# Revit family: 0048949
name_source: partatom
category: Lighting Fixtures
revit_build: Autodesk Revit 2017 (Build: 20190507_1515(x64)
units: mm (PartAtom-declared; Revit-internal decimal feet)

## family parameters
Cut with Voids When Loaded = No
Host = Face
Light Source = Yes
OmniClass Number = 23.80.70.00
OmniClass Title = Lighting
Part Type = Normal
Room Calculation Point = No
Round Connector Dimension = Use Diameter
Shared = No

## types (6) — shared parameters
Assembly Code = D5020200
AssetType = Fixed
ClassificationName = Uniclass2015
ClassificationValue = EF_70_80
Color Filter = 16777215
Default Elevation = 1219 mm
Dimming Lamp Color Temperature Shift = <None>
DocumentationLiterature = http://www.sylvania-lighting.com
ElectricShockClassification = Class I
Emit Shape Visible in Rendering = No
Emit from Circle Diameter = 610 mm
GAP_SYL = 3 mm  [stored 0.00984252 ft]
HEIGHT_SYL = 77 mm
HOLE_HEIGHT_SYL = 24 mm
IfcExportAs = IfcLightFixtureType
IfcExportType = IfcLightFixtureType
ImpactProtectionIndex = IK08
IngressProtection = IP20
Keynote = 16500
LUM_R_SYL = 30 mm  [stored 0.0984252 ft]
Lamp = LED
LampColourRenderingIndex = 80
LampColourTemperature = 4000 K
LampMacAdamStep = 5
LampsType = LED
Manufacturer = Feilo Sylvania
ManufacturerName = Feilo Sylvania
Material = steel housing, pc polycarbonate diffuser
Material_1_SYL = Dynamo
Material_2_SYL = <By Category>
Material_3_SYL = <By Category>
Material_4_SYL = <By Category>
NominalDepth = 70 mm
NominalHeight = 77 mm
NominalLength = 672 mm
PowerFactor = 0.9
R_HEIGHT_SYL = 44 mm
Tilt Angle = -90.00°
Type Image = <None>
URL = http://www.sylvania-lighting.com
Voltage = 0 V
WIDTH/2_SYL = 35 mm  [stored 0.114829 ft]
zero-valued in all types: Cost

## per-type parameters (varying)
| type | Apparent Load | Description | LampNominalLuminous | LuminousEfficacy | Model | ModelNumber | ModelReference | Name | Photometric Web File | PowerConsumption | TypeName | Weight |
| 0048951 WAYLINE 600 MWCOR 1200LM 840 | 10 VA | LED batten, T8 replacement, ease of installation through 2 part push-in design of the housing (safety cable included), through wiring capability, steel housing, 1200lm, 10W, 120lm/W, 4000K, CRI80, 3 step MacAdam ellipse, symmetric wide beam angle, Class I, 90000 hrs L80B20 lifespan, non-dimmable driver, corridor function with microwave presence sensor, IK08, IP20, 672 x 70 x 76.5mm  (L x W x H) dimensions, 1.1kg. | 1200 lm | 120 lm/W | Wayline 600 MWCOR 1200lm 840 | 48951 | Wayline 600 MWCOR 1200lm 840 | Wayline 600 MWCOR 1200lm 840 | 0048951.ies | 10 W | Wayline 600 MWCOR 1200lm 840 | 9.9 kg |
| 0048950 WAYLINE 600 MW 2900LM 840 | 22 VA | LED batten, T8 replacement, ease of installation through 2 part push-in design of the housing (safety cable included), through wiring capability, steel housing, 2900lm, 22W, 132lm/W, 4000K, CRI80, 3 step MacAdam ellipse, symmetric wide beam angle, Class I, 90000 hrs L80B20 lifespan, non-dimmable driver, MW sensor for 360° detection up to 8m range at 6m mounting height, IK08, IP20, 672 x 70 x 76.5mm (LxWxD) dimensions, 0.92kg weight. | 2900 lm | 132 lm/W | Wayline 600 MW 2900lm 840 | 48950 | Wayline 600 MW 2900lm 840 | Wayline 600 MW 2900lm 840 | 0048950.ies | 22 W | Wayline 600 MW 2900lm 840 | 8.28 kg |
| 0048949 WAYLINE 600 MW 1200LM 840 | 10 VA | LED batten, T8 replacement, ease of installation through 2 part push-in design of the housing (safety cable included), through wiring capability, steel housing, 1200lm, 10W, 120lm/W, 4000K, CRI80, 3 step MacAdam ellipse, symmetric wide beam angle, Class I, 90000 hrs L80B20 lifespan, non-dimmable driver, MW sensor for 360° detection up to 8m range at 6m mounting height, IK08, IP20, 672 x 70 x 76.5mm (LxWxD) dimensions, 0.87kg weight. | 1200 lm | 120 lm/W | Wayline 600 MW 1200lm 840 | 48949 | Wayline 600 MW 1200lm 840 | Wayline 600 MW 1200lm 840 | 0048949.ies | 10 W | Wayline 600 MW 1200lm 840 | 7.83 kg |
| 0048923 WAYLINE 600 DALI 2600LM 840 | 19 VA | LED batten, T8 replacement, ease of installation through 2 part push-in design of the housing (safety cable included), through wiring capability, steel housing, 2600lm, 19W, 137lm/W, 4000K, CRI80, 3 step MacAdam ellipse, symmetric wide beam angle, Class I, 90000 hrs L80B20 lifespan, DALI dimmable driver, IK08, IP20, 672 x 70 x 76.5mm (LxWxD) dimensions, 1.03kg weight. | 2600 lm | 137 lm/W | Wayline 600 DALI 2600lm 840 | 48923 | Wayline 600 DALI 2600lm 840 | Wayline 600 DALI 2600lm 840 | 0048923.ies | 19 W | Wayline 600 DALI 2600lm 840 | 9.27 kg |
| 0048922 WAYLINE 600 DALI 1200LM 840 | 9 VA | LED batten, T8 replacement, ease of installation through 2 part push-in design of the housing (safety cable included), through wiring capability, steel housing, 1200lm, 9W, 133lm/W, 4000K, CRI80, 3 step MacAdam ellipse, symmetric wide beam angle, Class I, 90000 hrs L80B20 lifespan, DALI dimmable driver, IK08, IP20, 672 x 70 x 76.5mm (LxWxD) dimensions, 1.03kg weight. | 1200 lm | 133 lm/W | Wayline 600 DALI 1200lm 840 | 48922 | Wayline 600 DALI 1200lm 840 | Wayline 600 DALI 1200lm 840 | 0048922.ies | 9 W | Wayline 600 DALI 1200lm 840 | 9.27 kg |
| 0048952 WAYLINE 600 MWCOR 2600LM 840 | 20 VA | LED batten, T8 replacement, ease of installation through 2 part push-in design of the housing (safety cable included), through wiring capability, steel housing, 2600lm, 20W, 130lm/W, 4000K, CRI80, 3 step MacAdam ellipse, symmetric wide beam angle, Class I, 90000 hrs L80B20 lifespan, non-dimmable driver, corridor function with microwave presence sensor, IK08, IP20, 672 x 70 x 76.5mm  (L x W x H) dimensions, 1.1kg. | 2600 lm | 130 lm/W | Wayline 600 MWCOR 2600lm 840 | 48952 | Wayline 600 MWCOR 2600lm 840 | Wayline 600 MWCOR 2600lm 840 | 0048952.ies | 20 W | Wayline 600 MWCOR 2600lm 840 | 9.9 kg |

note: [stored X ft] marks values corroborated as IEEE doubles in the binary element streams (Revit-internal decimal feet)

## geometry (parser evidence)
native form markers: Sweep x2
no freeform markers — native parametric forms only
